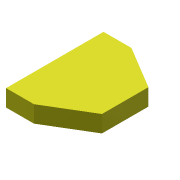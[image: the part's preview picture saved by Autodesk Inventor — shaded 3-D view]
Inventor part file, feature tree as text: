
AUTODESK INVENTOR PART (.ipt)
format: ipt  version: 2022 (Build 260153000, 153)  size: 200,192 bytes
history: native  units: mm
features: extrude x7, sketch x6, projected_geometry x6
ambient origin geometry x8: Origin, YZ Plane, XZ Plane, XY Plane, X Axis, Y Axis, Z Axis, Center Point
bodies: Solid1 (feature_tree)
feature tree (19):
  extrude  "Extrusion1"  Depth=8.0mm TaperAngle=360.0deg
  extrude  "Extrusion2"  Depth=5.0mm
  extrude  "Extrusion3"  Depth=5.0mm
  extrude  "Extrusion5"  Depth=3.0mm TaperAngle=0.0deg
  extrude  "Extrusion6"  Depth=1.5mm TaperAngle=0.0deg
  extrude  "Extrusion7"  Depth=1.0mm
  extrude  "Extrusion8"  Depth=1.0mm
  sketch  "Sketch1"  dims[d2=8.0mm d4=30.0mm d6=360.0deg]
  sketch  "Sketch2"  dims[d8=6.0mm d9=5.0mm]
  projected_geometry  "Projected Loop1"
  sketch  "Sketch3"  dims[d11=16.0mm d12=5.0mm]
  projected_geometry  "Projected Loop2"
  sketch  "Sketch5"  dims[d13=5.0mm d14=3.0mm d15=0.0mm]
  projected_geometry  "Projected Loop3"
  sketch  "Sketch6"  dims[d16=3.5mm d17=1.5mm d18=0.0mm]
  projected_geometry  "Projected Loop4"
  projected_geometry  "Projected Loop5"
  sketch  "Sketch8"  dims[d19=9.0mm d20=9.0mm d21=15.0mm d22=15.0mm d23=0.5mm d24=0.0mm d27=4.0mm d28=0.5mm d29=0.0mm d30=3.0mm d31=3.0mm d32=10.0mm d33=0.0mm d35=3.5mm d37=3.5mm d38=0.0mm d39=5.6mm d40=1.0mm d41=0.0mm]
  projected_geometry  "Projected Loop6"
